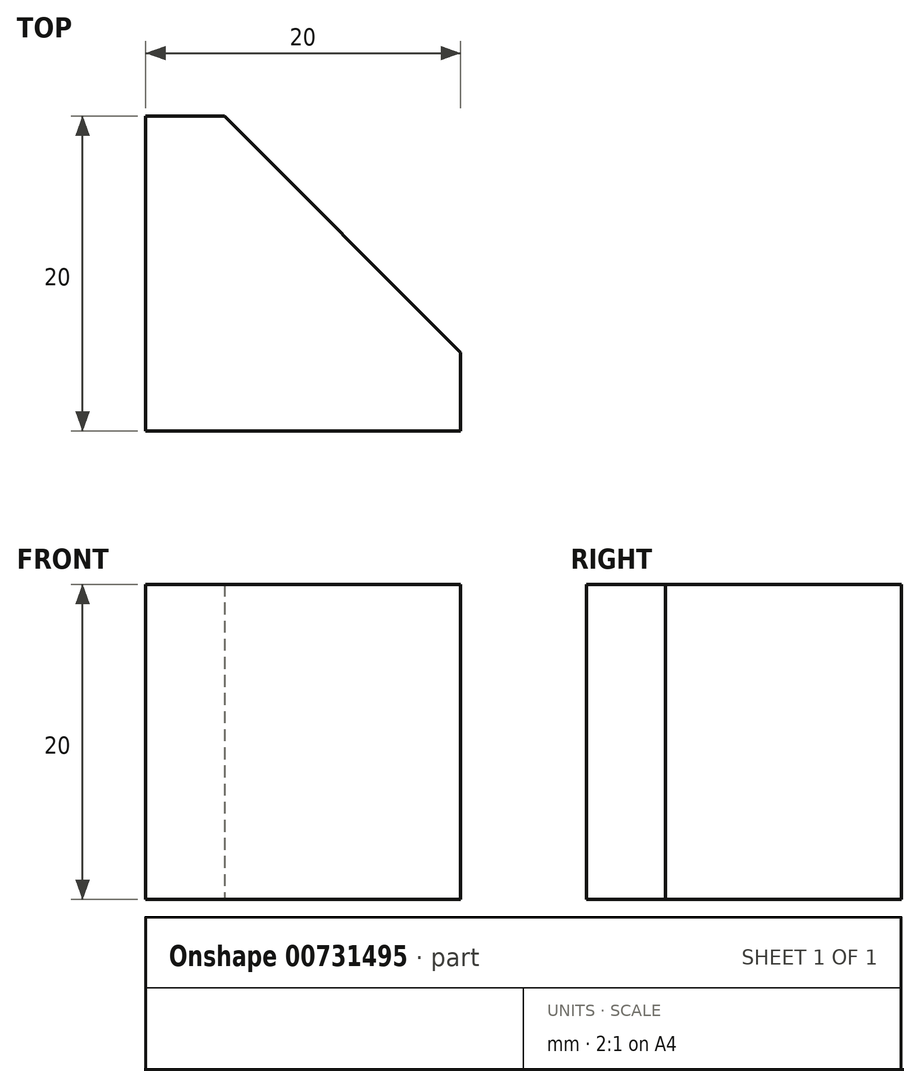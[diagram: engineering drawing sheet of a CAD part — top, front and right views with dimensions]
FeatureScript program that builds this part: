
annotation { "Feature Type Name" : "Feature", "Feature Type Description" : "" }
export const myFeature = defineFeature(function(context is Context, id is Id, definition is map)
    precondition{}
    {
        {
            var Q0;
            Q0=qCreatedBy(makeId("Top.planeOp"),FACE);
            var sketch = newSketch(context, id + "F0", { "sketchPlane" : qUnion([Q0])});
            skLineSegment(sketch, "E0.bottom", {"start": v(0, 0) * mm, "end": v(20, 0) * mm});
            skLineSegment(sketch, "E0.top", {"start": v(0, 20) * mm, "end": v(5, 20) * mm});
            skLineSegment(sketch, "E0.left", {"start": v(0, 0) * mm, "end": v(0, 20) * mm});
            skLineSegment(sketch, "E0.right", {"start": v(20, 0) * mm, "end": v(20, 5) * mm});
            skLineSegment(sketch, "E1", {"start": v(5, 20) * mm, "end": v(20, 5) * mm});
            skSolve(sketch);
        }
        {
            var Q0;
            Q0=qSketchRegion(id+"F0",true);
            extrude(context, id + "F1", {"entities" : qUnion([Q0]), "depth" : 20 * mm, "offsetDistance" : 25 * mm});
        }
    });
